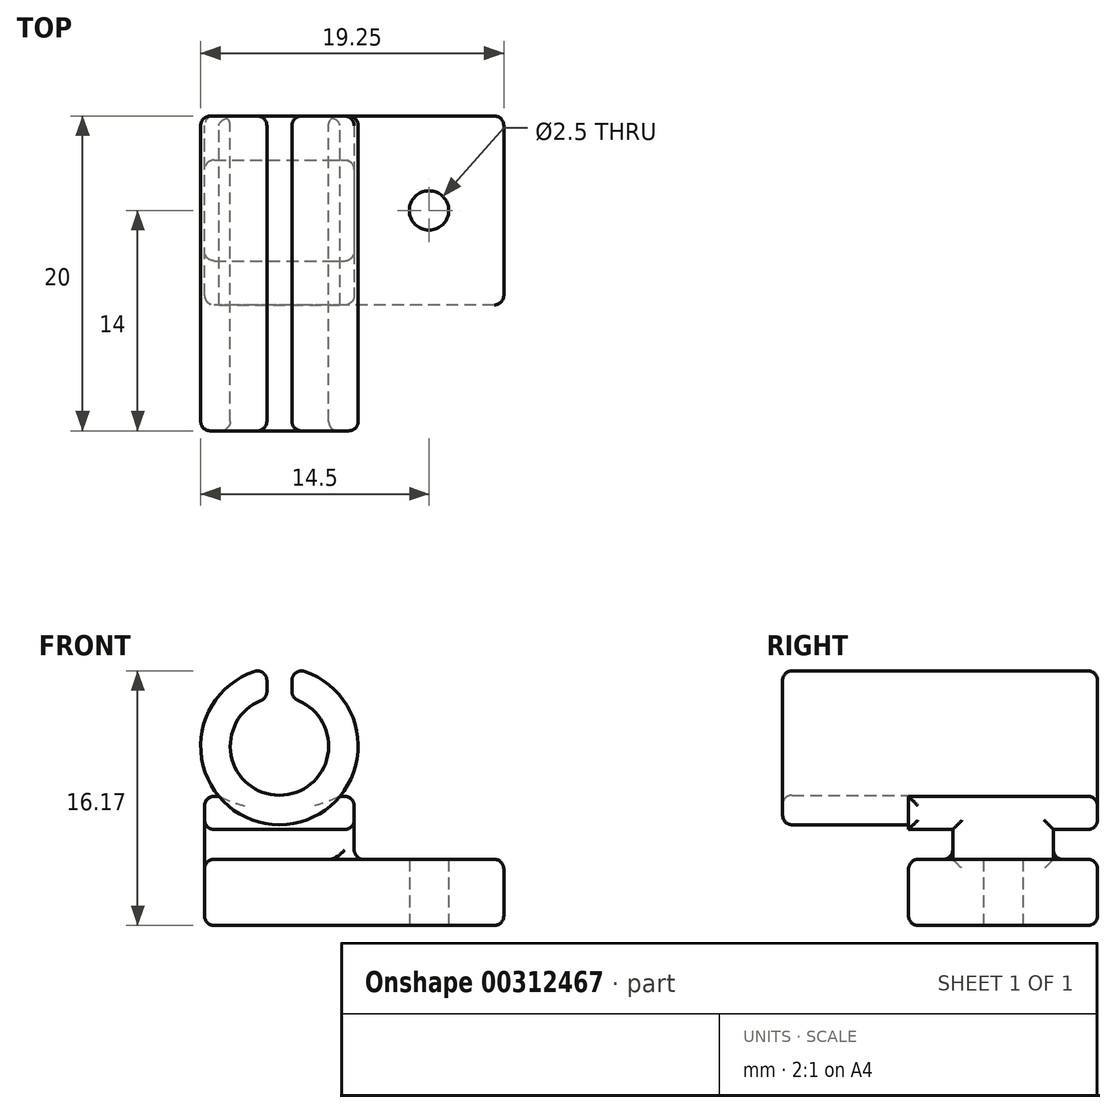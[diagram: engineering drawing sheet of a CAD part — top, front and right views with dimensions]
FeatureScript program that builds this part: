
annotation { "Feature Type Name" : "Feature", "Feature Type Description" : "" }
export const myFeature = defineFeature(function(context is Context, id is Id, definition is map)
    precondition{}
    {
        {
            var Q0;
            Q0=qCreatedBy(makeId("Top.planeOp"),FACE);
            var sketch = newSketch(context, id + "F0", { "sketchPlane" : qUnion([Q0])});
            skLineSegment(sketch, "E0.bottom", {"start": v(9.5, -6) * mm, "end": v(-9.5, -6) * mm});
            skLineSegment(sketch, "E0.top", {"start": v(9.5, 6) * mm, "end": v(-9.5, 6) * mm});
            skLineSegment(sketch, "E0.left", {"start": v(9.5, -6) * mm, "end": v(9.5, 6) * mm});
            skLineSegment(sketch, "E0.right", {"start": v(-9.5, -6) * mm, "end": v(-9.5, 6) * mm});
            skPoint(sketch, "E0.middle", {"position": v(0, 0) * mm});
            skLineSegment(sketch, "E1.bottom", {"start": v(-9.5, 6) * mm, "end": v(0, 6) * mm});
            skLineSegment(sketch, "E1.top", {"start": v(-9.5, -6) * mm, "end": v(0, -6) * mm});
            skLineSegment(sketch, "E1.left", {"start": v(-9.5, 6) * mm, "end": v(-9.5, -6) * mm});
            skLineSegment(sketch, "E1.right", {"start": v(0, 6) * mm, "end": v(0, -6) * mm});
            skLineSegment(sketch, "E2.bottom", {"start": v(-9.5, 3.2) * mm, "end": v(0, 3.2) * mm});
            skLineSegment(sketch, "E2.top", {"start": v(-9.5, -3.2) * mm, "end": v(0, -3.2) * mm});
            skLineSegment(sketch, "E2.left", {"start": v(-9.5, 3.2) * mm, "end": v(-9.5, -3.2) * mm});
            skLineSegment(sketch, "E2.right", {"start": v(0, 3.2) * mm, "end": v(0, -3.2) * mm});
            skCircle(sketch, "E3", {"center": v(4.75, 0) * mm, "radius": 1.25 * mm});
            skSolve(sketch);
        }
        {
            var Q0;
            {var subQ2=sQuery(id+"F0.wireOp",EDGE,"E2.bottom");Q0=makeQuery(id+"F0.imprint","IMPRINT",FACE,{"disambiguationData":[TD([[makeQuery(id+"F0.imprint","IMPRINT",EDGE,{"derivedFrom":subQ2}),-1.0]])]});}
            var Q1;
            Q1=makeQuery(id+"F0.imprint","IMPRINT",FACE,{"disambiguationData":[TD([[makeQuery(id+"F0.imprint","IMPRINT",EDGE,{"derivedFrom":sQuery(id+"F0.wireOp",EDGE,"E3")}),1.0]])]});
            var Q2;
            {var subQ3=sQuery(id+"F0.wireOp",EDGE,"E0.left");Q2=makeQuery(id+"F0.imprint","IMPRINT",FACE,{"disambiguationData":[TD([[makeQuery(id+"F0.imprint","IMPRINT",EDGE,{"derivedFrom":subQ3}),1.0]])]});}
            var Q3;
            {var subQ5=sQuery(id+"F0.wireOp",EDGE,"E2.top");Q3=makeQuery(id+"F0.imprint","IMPRINT",FACE,{"disambiguationData":[TD([[makeQuery(id+"F0.imprint","IMPRINT",EDGE,{"derivedFrom":subQ5}),-1.0]])]});}
            var Q4;
            {var subQ5=sQuery(id+"F0.wireOp",EDGE,"E2.bottom");Q4=makeQuery(id+"F0.imprint","IMPRINT",FACE,{"disambiguationData":[TD([[makeQuery(id+"F0.imprint","IMPRINT",EDGE,{"derivedFrom":subQ5}),1.0]])]});}
            extrude(context, id + "F1", {"entities" : qUnion([Q0, Q1, Q2, Q3, Q4]), "oppositeDirection" : true, "depth" : 4.2 * mm, "offsetDistance" : 25 * mm});
        }
        {
            var Q0;
            {var subQ2=sQuery(id+"F0.wireOp",EDGE,"E2.bottom");Q0=makeQuery(id+"F0.imprint","IMPRINT",FACE,{"disambiguationData":[TD([[makeQuery(id+"F0.imprint","IMPRINT",EDGE,{"derivedFrom":subQ2}),-1.0]])]});}
            extrude(context, id + "F2", {"entities" : qUnion([Q0]), "operationType" : NewBodyOperationType.ADD, "depth" : 4 * mm, "offsetDistance" : 25 * mm});
        }
        {
            var Q0;
            {var subQ5=sQuery(id+"F0.wireOp",EDGE,"E2.bottom");Q0=makeQuery(id+"F0.imprint","IMPRINT",FACE,{"disambiguationData":[TD([[makeQuery(id+"F0.imprint","IMPRINT",EDGE,{"derivedFrom":subQ5}),1.0]])]});}
            var Q1;
            {var subQ5=sQuery(id+"F0.wireOp",EDGE,"E2.top");Q1=makeQuery(id+"F0.imprint","IMPRINT",FACE,{"disambiguationData":[TD([[makeQuery(id+"F0.imprint","IMPRINT",EDGE,{"derivedFrom":subQ5}),-1.0]])]});}
            extrude(context, id + "F3", {"entities" : qUnion([Q0, Q1]), "operationType" : NewBodyOperationType.ADD, "depth" : 4 * mm, "offsetDistance" : 25 * mm, "hasSecondDirection" : true, "secondDirectionOppositeDirection" : false, "secondDirectionDepth" : 1.9 * mm});
        }
        {
            var Q0;
            Q0=sQuery(id+"F0.wireOp",VERTEX,"E3.center");
            var Q1;
            Q1=makeQuery(id+"F1.opExtrude","SWEPT_BODY",BODY,{"disambiguationData":[OSD([sQuery(id+"F0.wireOp",EDGE,"E0.bottom"),sQuery(id+"F0.wireOp",EDGE,"E0.top"),sQuery(id+"F0.wireOp",EDGE,"E0.left"),sQuery(id+"F0.wireOp",EDGE,"E0.right")])]});
            hole(context, id + "F4", {"style" : HoleStyle.SIMPLE, "endStyle" : HoleEndStyle.THROUGH, "standardTappedOrClearance" : lookupTablePath({ "standard" : "ISO", "engagement" : "75%", "pitch" : "0.5 mm", "size" : "M3", "type" : "Tapped" }), "standardBlindInLast" : lookupTablePath({ "standard" : "ISO", "engagement" : "75%", "pitch" : "0.5 mm", "size" : "M3", "type" : "Tapped" }), "holeDiameter" : 2.5 * mm, "majorDiameter" : 3 * mm, "showTappedDepth" : true, "isTappedThrough" : true, "tappedDepth" : 12 * mm, "tapClearance" : 3, "locations" : qUnion([Q0]), "scope" : qUnion([Q1]), "startStyle" : HoleStartStyle.SKETCH});
        }
        {
            var Q0;
            Q0=makeQuery(id+"F1.opExtrude","SWEPT_FACE",FACE,{"disambiguationData":[OSD([sQuery(id+"F0.wireOp",EDGE,"E0.top")])]});
            var sketch = newSketch(context, id + "F5", { "sketchPlane" : qUnion([Q0])});
            skArc(sketch, "E4", {"start": v(3.95, 12.14) * mm, "mid": v(4.75, 2.2) * mm, "end": v(5.55, 12.14) * mm});
            skArc(sketch, "E5", {"start": v(3.95, 10.22) * mm, "mid": v(4.75, 4.07) * mm, "end": v(5.55, 10.22) * mm});
            skLineSegment(sketch, "E6.left", {"start": v(3.95, 12.14) * mm, "end": v(3.95, 10.22) * mm});
            skLineSegment(sketch, "E6.right", {"start": v(5.55, 12.14) * mm, "end": v(5.55, 10.22) * mm});
            skSolve(sketch);
        }
        {
            var Q0;
            Q0=makeQuery(id+"F5.imprint","IMPRINT",FACE,{"disambiguationData":[TD([[makeQuery(id+"F5.imprint","IMPRINT",EDGE,{"derivedFrom":sQuery(id+"F5.wireOp",EDGE,"E4")}),1.0]])]});
            extrude(context, id + "F6", {"entities" : qUnion([Q0]), "operationType" : NewBodyOperationType.ADD, "oppositeDirection" : true, "depth" : 20 * mm, "offsetDistance" : 25 * mm});
        }
        {
            var Q0;
            Q0=makeQuery(id+"F6.boolean.opBoolean","MERGE",FACE,{"derivedFrom":[makeQuery(id+"F3.opExtrude","SWEPT_FACE",FACE,{"disambiguationData":[OSD([sQuery(id+"F0.wireOp",EDGE,"E0.top")])]}),makeQuery(id+"F6.opExtrude","CAP_FACE",FACE,{"disambiguationData":[OSD([sQuery(id+"F5.wireOp",EDGE,"E4"),sQuery(id+"F5.wireOp",EDGE,"E5"),sQuery(id+"F5.wireOp",EDGE,"E6.left"),sQuery(id+"F5.wireOp",EDGE,"E6.right")])],"isStart":true})]});
            var Q1;
            Q1=makeQuery(id+"F6.opExtrude","CAP_FACE",FACE,{"disambiguationData":[OSD([sQuery(id+"F5.wireOp",EDGE,"E4"),sQuery(id+"F5.wireOp",EDGE,"E5"),sQuery(id+"F5.wireOp",EDGE,"E6.left"),sQuery(id+"F5.wireOp",EDGE,"E6.right")])],"isStart":false});
            var Q2;
            Q2=makeQuery(id+"F6.opExtrude","SWEPT_FACE",FACE,{"disambiguationData":[OSD([sQuery(id+"F5.wireOp",EDGE,"E6.left")])]});
            var Q3;
            Q3=makeQuery(id+"F6.opExtrude","SWEPT_FACE",FACE,{"disambiguationData":[OSD([sQuery(id+"F5.wireOp",EDGE,"E6.right")])]});
            var Q4;
            Q4=makeQuery(id+"F1.opExtrude","SWEPT_FACE",FACE,{"disambiguationData":[OSD([sQuery(id+"F0.wireOp",EDGE,"E0.bottom")])]});
            var Q5;
            Q5=makeQuery(id+"F1.opExtrude","SWEPT_FACE",FACE,{"disambiguationData":[OSD([sQuery(id+"F0.wireOp",EDGE,"E0.top")])]});
            var Q6;
            {var subQ0=sQuery(id+"F0.wireOp",EDGE,"E0.right");Q6=makeQuery(id+"F3.boolean.opBoolean","MERGE",FACE,{"derivedFrom":[makeQuery(id+"F2.boolean.opBoolean","MERGE",FACE,{"derivedFrom":[makeQuery(id+"F1.opExtrude","SWEPT_FACE",FACE,{"disambiguationData":[OSD([subQ0])]}),makeQuery(id+"F2.opExtrude","SWEPT_FACE",FACE,{"disambiguationData":[OSD([subQ0])]})]}),makeQuery(id+"F3.opExtrude","SWEPT_FACE",FACE,{"disambiguationData":[OSD([subQ0]),TDD([makeQuery(id+"F0.imprint","IMPRINT",EDGE,{"disambiguationData":[TD([[makeQuery(id+"F0.imprint","INTERSECT",VERTEX,{"derivedFrom":[sQuery(id+"F0.wireOp",EDGE,"E0.top"),subQ0]}),1.0]])],"derivedFrom":subQ0})])]}),makeQuery(id+"F3.opExtrude","SWEPT_FACE",FACE,{"disambiguationData":[OSD([subQ0]),TDD([makeQuery(id+"F0.imprint","IMPRINT",EDGE,{"disambiguationData":[TD([[makeQuery(id+"F0.imprint","INTERSECT",VERTEX,{"derivedFrom":[sQuery(id+"F0.wireOp",EDGE,"E0.bottom"),subQ0]}),-1.0]])],"derivedFrom":subQ0})])]})]});}
            var Q7;
            Q7=makeQuery(id+"F1.opExtrude","SWEPT_FACE",FACE,{"disambiguationData":[OSD([sQuery(id+"F0.wireOp",EDGE,"E0.left")])]});
            var Q8;
            {var subQ0=sQuery(id+"F0.wireOp",EDGE,"E1.right");Q8=makeQuery(id+"F3.boolean.opBoolean","MERGE",FACE,{"derivedFrom":[makeQuery(id+"F2.opExtrude","SWEPT_FACE",FACE,{"disambiguationData":[OSD([subQ0])]}),makeQuery(id+"F3.opExtrude","SWEPT_FACE",FACE,{"disambiguationData":[OSD([subQ0]),TDD([makeQuery(id+"F0.imprint","IMPRINT",EDGE,{"disambiguationData":[TD([[makeQuery(id+"F0.imprint","INTERSECT",VERTEX,{"derivedFrom":[subQ0,sQuery(id+"F0.wireOp",EDGE,"E2.bottom")]}),1.0]])],"derivedFrom":subQ0})])]}),makeQuery(id+"F3.opExtrude","SWEPT_FACE",FACE,{"disambiguationData":[OSD([subQ0]),TDD([makeQuery(id+"F0.imprint","IMPRINT",EDGE,{"disambiguationData":[TD([[makeQuery(id+"F0.imprint","INTERSECT",VERTEX,{"derivedFrom":[sQuery(id+"F0.wireOp",EDGE,"E0.bottom"),subQ0]}),1.0]])],"derivedFrom":subQ0})])]})]});}
            fillet(context, id + "F7", {"entities" : qUnion([Q0, Q1, Q2, Q3, Q4, Q5, Q6, Q7, Q8]), "radius" : 0.6 * mm, "tangentPropagation" : true, "allowEdgeOverflow" : false});
        }
    });
